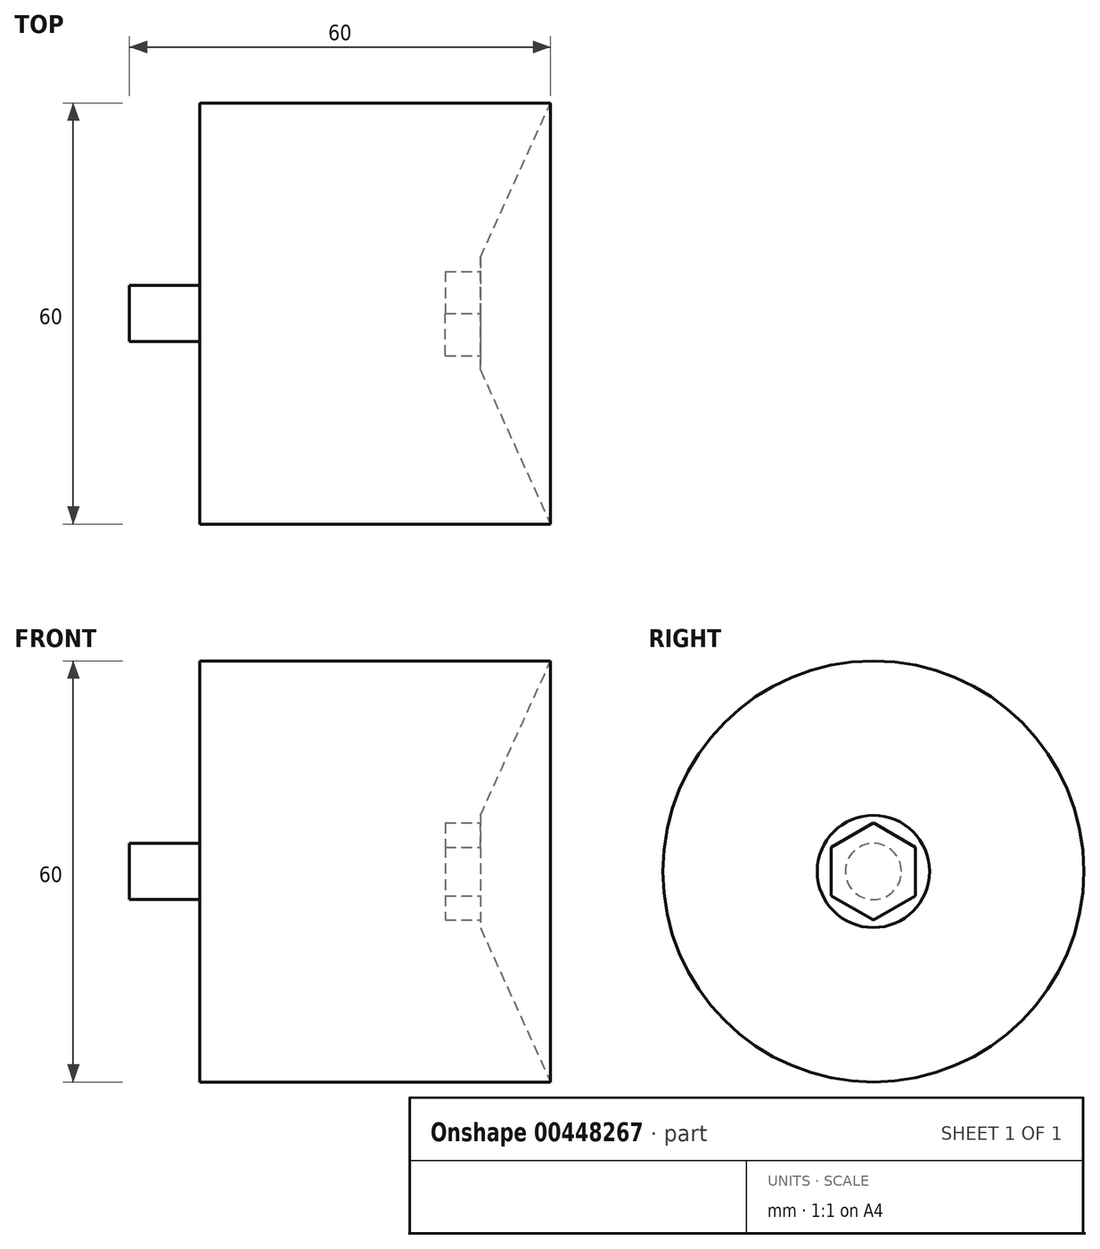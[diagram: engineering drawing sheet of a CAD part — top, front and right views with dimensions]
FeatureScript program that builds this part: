
annotation { "Feature Type Name" : "Feature", "Feature Type Description" : "" }
export const myFeature = defineFeature(function(context is Context, id is Id, definition is map)
    precondition{}
    {
        {
            var Q0;
            Q0=qCreatedBy(makeId("Front.planeOp"),FACE);
            var sketch = newSketch(context, id + "F0", { "sketchPlane" : qUnion([Q0])});
            skLineSegment(sketch, "E0", {"start": v(-40, 30) * mm, "end": v(-40, 0) * mm});
            skLineSegment(sketch, "E1", {"start": v(-40, 0) * mm, "end": v(0, 0) * mm});
            skLineSegment(sketch, "E2", {"start": v(0, 0) * mm, "end": v(0, 8) * mm});
            skLineSegment(sketch, "E3", {"start": v(0, 8) * mm, "end": v(10, 30) * mm});
            skLineSegment(sketch, "E4", {"start": v(10, 30) * mm, "end": v(-40, 30) * mm});
            skLineSegment(sketch, "E5", {"start": v(-74.95, 0) * mm, "end": v(69.14, 0) * mm, "construction": true});
            skSolve(sketch);
        }
        {
            var Q0;
            Q0=makeQuery(id+"F0.imprint","IMPRINT",FACE,{"disambiguationData":[TD([[makeQuery(id+"F0.imprint","IMPRINT",EDGE,{"derivedFrom":sQuery(id+"F0.wireOp",EDGE,"E0")}),1.0]])]});
            var Q1;
            Q1=sQuery(id+"F0.wireOp",EDGE,"E5");
            revolve(context, id + "F1", {"entities" : qUnion([Q0]), "axis" : qUnion([Q1]), "revolveType" : RevolveType.FULL});
        }
        {
            var Q0;
            Q0=makeQuery(id+"F1.opRevolve","SWEPT_FACE",FACE,{"disambiguationData":[OSD([sQuery(id+"F0.wireOp",EDGE,"E2")])]});
            var sketch = newSketch(context, id + "F2", { "sketchPlane" : qUnion([Q0])});
            skCircle(sketch, "E6.cCircle", {"center": v(0, 0) * mm, "radius": 6 * mm, "construction": true});
            skLineSegment(sketch, "E6.0", {"start": v(6, -3.46) * mm, "end": v(0, -6.93) * mm});
            skLineSegment(sketch, "E6.1", {"start": v(0, -6.93) * mm, "end": v(-6, -3.46) * mm});
            skLineSegment(sketch, "E6.2", {"start": v(-6, -3.46) * mm, "end": v(-6, 3.46) * mm});
            skLineSegment(sketch, "E6.3", {"start": v(-6, 3.46) * mm, "end": v(0, 6.93) * mm});
            skLineSegment(sketch, "E6.4", {"start": v(0, 6.93) * mm, "end": v(6, 3.46) * mm});
            skLineSegment(sketch, "E6.5", {"start": v(6, 3.46) * mm, "end": v(6, -3.46) * mm});
            skPoint(sketch, "E6.0.midPoint", {"position": v(3, -5.2) * mm});
            skSolve(sketch);
        }
        {
            var Q0;
            Q0=makeQuery(id+"F2.imprint","IMPRINT",FACE,{"disambiguationData":[TD([[makeQuery(id+"F2.imprint","IMPRINT",EDGE,{"derivedFrom":sQuery(id+"F2.wireOp",EDGE,"E6.0")}),-1.0]])]});
            extrude(context, id + "F3", {"entities" : qUnion([Q0]), "operationType" : NewBodyOperationType.REMOVE, "oppositeDirection" : true, "depth" : 5 * mm});
        }
        {
            var Q0;
            Q0=makeQuery(id+"F1.opRevolve","SWEPT_FACE",FACE,{"disambiguationData":[OSD([sQuery(id+"F0.wireOp",EDGE,"E0")])]});
            var sketch = newSketch(context, id + "F4", { "sketchPlane" : qUnion([Q0])});
            skCircle(sketch, "E7", {"center": v(0, 0) * mm, "radius": 4 * mm});
            skSolve(sketch);
        }
        {
            var Q0;
            Q0=makeQuery(id+"F4.imprint","IMPRINT",FACE,{"disambiguationData":[TD([[makeQuery(id+"F4.imprint","IMPRINT",EDGE,{"derivedFrom":sQuery(id+"F4.wireOp",EDGE,"E7")}),1.0]])]});
            extrude(context, id + "F5", {"entities" : qUnion([Q0]), "operationType" : NewBodyOperationType.ADD, "depth" : 10 * mm});
        }
    });
